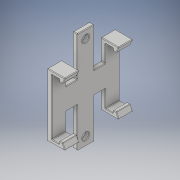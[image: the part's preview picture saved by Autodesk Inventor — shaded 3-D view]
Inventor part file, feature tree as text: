
AUTODESK INVENTOR PART (.ipt)
format: ipt  version: 2019 (Build 230136000, 136)  size: 390,656 bytes
history: native  units: in
note: dims shown in document units (in); Inventor stores cm internally (conversion verified against a paired STEP export)
features: extrude x7, sketch x7, plane x3, mirror x3, fillet x1, projected_geometry x1
ambient origin geometry x8: Origin, YZ Plane, XZ Plane, XY Plane, X Axis, Y Axis, Z Axis, Center Point
bodies: Solid1 (feature_tree)
feature tree (22):
  extrude  "Extrusion1"  Depth=0.5118in
  extrude  "Extrusion2"  Depth=0.5118in
  extrude  "Extrusion3"  Depth=0.2717in TaperAngle=0.0deg
  extrude  "Extrusion4"  Depth=0.0866in
  plane  "Work Plane2"
  mirror  "Mirror1"
  extrude  "Extrusion5"  Depth=0.1181in
  plane  "Work Plane3"
  mirror  "Mirror2"
  extrude  "Extrusion6"  Depth=0.7874in
  extrude  "Extrusion7"  Depth=0.1575in
  plane  "Work Plane4"
  mirror  "Mirror3"
  fillet  "Fillet1"  Radius=0.5906in
  sketch  "Sketch1"  dims[d0=2.0157in d1=0.5118in]
  sketch  "Sketch3"  dims[d2=0.1575in d3=0.0in d4=0.5118in]
  sketch  "Sketch4"  dims[d5=0.1181in d6=0.2717in d7=0.0in]
  projected_geometry  "Projected Loop1"
  sketch  "Sketch5"  dims[d8=0.1575in d9=0.0in d10=0.0866in]
  sketch  "Sketch6"  dims[d11=0.1181in d12=0.4535in]
  sketch  "Sketch7"  dims[d13=0.1575in d14=0.0in d15=0.7874in]
  sketch  "Sketch8"  dims[d16=1.4173in d17=0.0in d18=0.1575in d19=0.5906in d20=1.4173in d21=0.0in d22=0.248in d23=1.4173in d24=0.0in d25=0.0197in]
